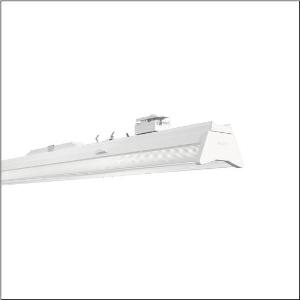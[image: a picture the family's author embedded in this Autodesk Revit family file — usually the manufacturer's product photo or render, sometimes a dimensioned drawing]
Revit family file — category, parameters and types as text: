
# Revit family: licross_21_performance_ho_52tm16cn4c5m
name_source: partatom
category: Lighting Fixtures
units: mm (PartAtom-declared; Revit-internal decimal feet)

## family parameters
Cut with Voids When Loaded = No
Host = Face
Light Source = No
Part Type = Normal
Room Calculation Point = No
Round Connector Dimension = Use Diameter
Shared = No

## types (1)
- --- (1 x LED, 12610 lm, 68.9 W, 4000K)
    Apparent Load = 69 VA
    CIE Flux Codes = 63 87 95 78 100
    Color Rendering = 80
    Color Temperature = 4000K
    Default Elevation = 1800 mm
    Description = Licross 21 Performance HO, luminaire insert, of sheet steel, galvanised, coil coated, white, length: 1.500mm, width: 120mm, height: 123mm, LED rated luminous flux: 12.610lm, light colour: 840, SDCM (Standard Deviation of Colour Matching)MacAdam ≤ 3 SDCM (initial), control gear: ON/OFF Multilumen, CLOi, with plug, 3-pole, with phase selection, mains connection: 220..240V, AC, 50/60Hz, start of lifetime: 69W, end of service life: 83W, internal wiring halogen-free, primary light control with lens, of plastic, primary optical cover: cover, of PMMA, light emission: direct/indirect distribution, primary light characteristic: symmetric, protection rating (complete): IP40, insulation class (complete): insulation class I (protective earthing), certification: CE, ENEC, UKCA, protection symbol: D if used in an environment without relevant dust loads with corresponding accessories, impact resistance: IK06, permissible ambient temperature for indoor applications: -35..+35°C, corresponds to IFS (International Featured Standards) requirements for safety and quality in the food industry, reducing of maximum allowable ambient temperature of 5°C with ceiling mounting, LABS conformity tested according to VDMA 24364:2018-05, The light source and the operating device comply with the requirements of the Ecodesign Regulation (EU) 2019/2020 and are replaceable in accordance with this regulation, packaging unit: 1 piece
    Height = 114 mm
    Lamp = 1 x LED
    Lamp Light Flux = 12610 lm
    Lamp Power = 68.9 W
    Lamp count = 1
    Length = 1500 mm
    Luminous efficacy = 183 lm/W
    Manufacturer = Siteco
    ModVariant = No
    Model = 52TM16CN4C5M
    Mounting Place = Ceiling
    Mounting Type = Pendant
    Number of Poles = 1
    OnlyDefault = Yes
    Power Factor = 1
    Product Name = Licross 21 Performance HO
    Product group = luminaire insert | ceiling pendant
    ProductGroupID = 901
    Protection Class = Protection class I
    Protection Degree = IP 40
    RLX_Detail_Level = 1
    RLX_Emergency_Light_Flux = 0 lm
    RLX_Emergency_Type = 0
    RLX_Emergency_Type_DB = No
    RlxData = <blob elided: 32085 chars, md5=cc94f6d6>
    Socket = socket
    Standby Power = 0 W
    System Light Flux = 12610 lm
    System Power = 69 W
    Type Comments = factory setting: luminous flux: 100 % | (A | C | E) | 162 mA
    Type Image = l_1256138.jpg
    URL = http://relux.com
    VarID = @adj_113133
    Voltage = 0 V
    Weight = 0.00 kg
    Width = 120 mm

## geometry (parser evidence)
native form markers: Blend x4, Sweep x13
no freeform markers — native parametric forms only
